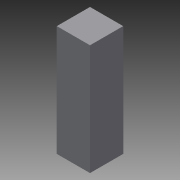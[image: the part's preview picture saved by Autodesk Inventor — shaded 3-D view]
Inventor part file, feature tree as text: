
AUTODESK INVENTOR PART (.ipt)
format: ipt  version: 2015 (Build 190159000, 159)  size: 78,848 bytes
history: native  units: in
note: dims shown in document units (in); Inventor stores cm internally (conversion verified against a paired STEP export)
features: extrude x2, sketch x2
ambient origin geometry x8: Origin, YZ Plane, XZ Plane, XY Plane, X Axis, Y Axis, Z Axis, Center Point
bodies: Solid1 (feature_tree)
feature tree (4):
  extrude  "Extrusion1"  Depth=0.75in
  extrude  "Extrusion2"  Depth=4.0in
  sketch  "Sketch1"  dims[d0=0.75in d1=0.75in]
  sketch  "Sketch2"  dims[d2=4.0in d3=0.0in d4=0.25in d5=2.5in d6=0.0in]
